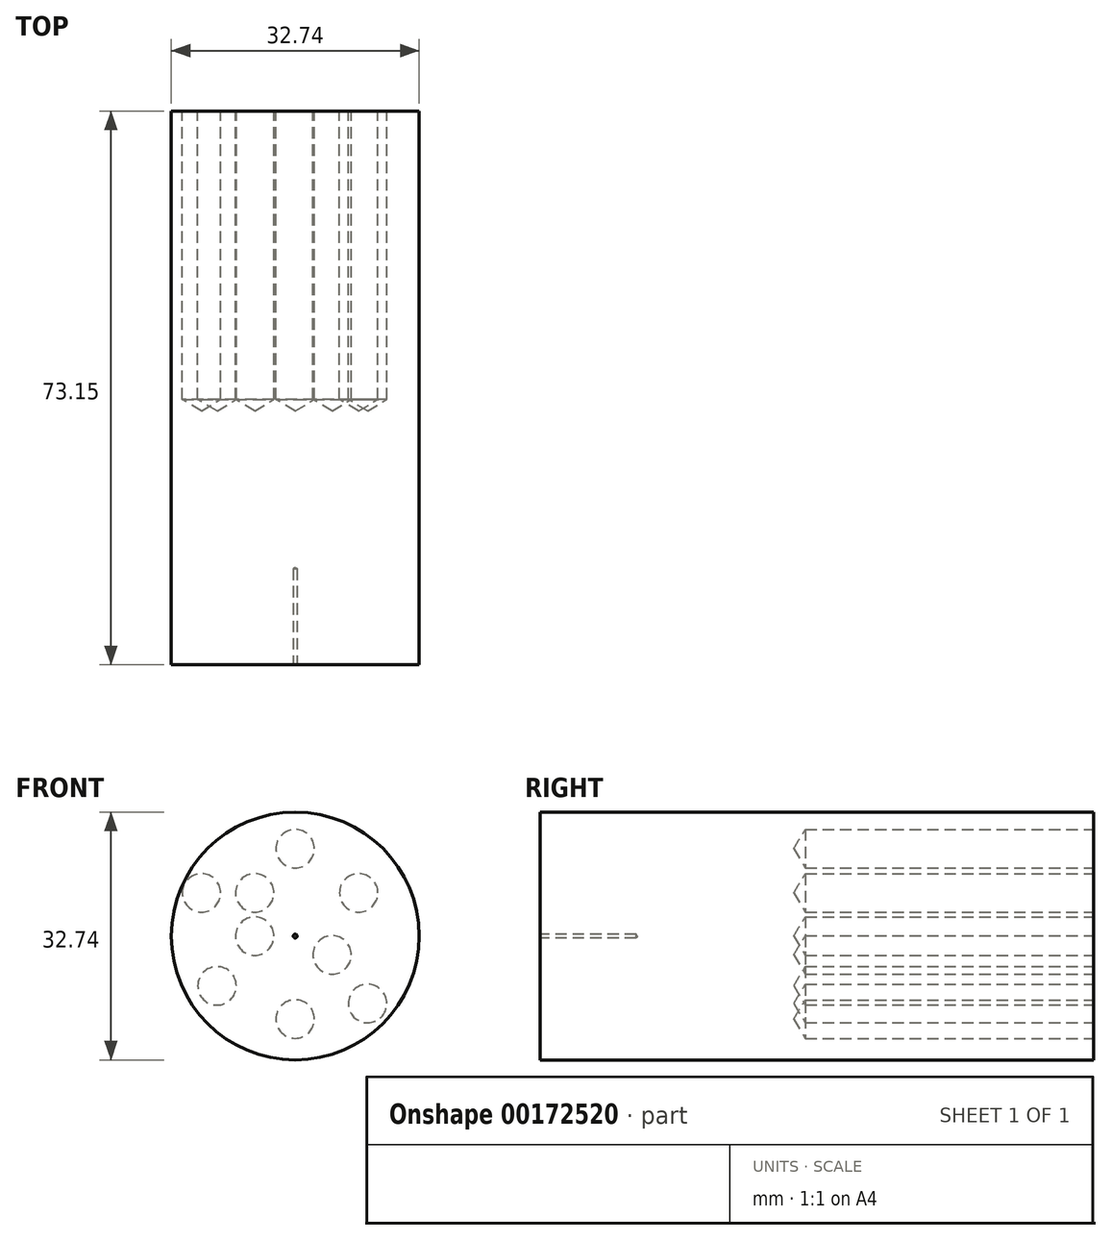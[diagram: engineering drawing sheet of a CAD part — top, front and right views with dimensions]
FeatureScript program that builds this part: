
annotation { "Feature Type Name" : "Feature", "Feature Type Description" : "" }
export const myFeature = defineFeature(function(context is Context, id is Id, definition is map)
    precondition{}
    {
        {
            var Q0;
            Q0=qCreatedBy(makeId("Front.planeOp"),FACE);
            var sketch = newSketch(context, id + "F0", { "sketchPlane" : qUnion([Q0])});
            skCircle(sketch, "E0", {"center": v(0, 0) * mm, "radius": 16.37 * mm});
            skSolve(sketch);
        }
        {
            var Q0;
            Q0=makeQuery(id+"F0.imprint","IMPRINT",FACE,{"disambiguationData":[TD([[makeQuery(id+"F0.imprint","IMPRINT",EDGE,{"derivedFrom":sQuery(id+"F0.wireOp",EDGE,"E0")}),1.0]])]});
            extrude(context, id + "F1", {"entities" : qUnion([Q0]), "depth" : 73.15 * mm});
        }
        {
            var Q0;
            Q0=makeQuery(id+"F1.opExtrude","CAP_FACE",FACE,{"disambiguationData":[OSD([sQuery(id+"F0.wireOp",EDGE,"E0")])],"isStart":false});
            var sketch = newSketch(context, id + "F2", { "sketchPlane" : qUnion([Q0])});
            skCircle(sketch, "E1", {"center": v(0, 0) * mm, "radius": 16.43 * mm});
            skSolve(sketch);
        }
        {
            var Q0;
            Q0=sQuery(id+"F2.wireOp",VERTEX,"E1.center");
            var Q1;
            Q1=makeQuery(id+"F1.opExtrude","SWEPT_BODY",BODY,{"disambiguationData":[OSD([sQuery(id+"F0.wireOp",EDGE,"E0")])]});
            hole(context, id + "F3", {"style" : HoleStyle.SIMPLE, "endStyle" : HoleEndStyle.BLIND, "holeDiameter" : 0.5 * mm, "holeDepth" : 12.7 * mm, "locations" : qUnion([Q0]), "scope" : qUnion([Q1])});
        }
        {
            var Q0;
            Q0=qCreatedBy(makeId("Front.planeOp"),FACE);
            var sketch = newSketch(context, id + "F4", { "sketchPlane" : qUnion([Q0])});
            skCircle(sketch, "E2", {"center": v(-5.36, 5.7) * mm, "radius": 5.2 * mm});
            skCircle(sketch, "E3", {"center": v(8.39, 5.7) * mm, "radius": 5.75 * mm});
            skCircle(sketch, "E4", {"center": v(4.88, -2.49) * mm, "radius": 7.96 * mm});
            skCircle(sketch, "E5", {"center": v(0, -10.97) * mm, "radius": 5.18 * mm});
            skCircle(sketch, "E6", {"center": v(9.56, -8.92) * mm, "radius": 4.37 * mm});
            skCircle(sketch, "E7", {"center": v(-5.36, 0) * mm, "radius": 5.15 * mm});
            skCircle(sketch, "E8", {"center": v(-10.34, -6.58) * mm, "radius": 6.05 * mm});
            skCircle(sketch, "E9", {"center": v(0, 11.56) * mm, "radius": 4.48 * mm});
            skCircle(sketch, "E10", {"center": v(-12.38, 5.7) * mm, "radius": 3.9 * mm});
            skSolve(sketch);
        }
        {
            var Q0;
            Q0=sQuery(id+"F4.wireOp",VERTEX,"E10.center");
            var Q1;
            Q1=sQuery(id+"F4.wireOp",VERTEX,"E2.center");
            var Q2;
            Q2=sQuery(id+"F4.wireOp",VERTEX,"E9.center");
            var Q3;
            Q3=sQuery(id+"F4.wireOp",VERTEX,"E3.center");
            var Q4;
            Q4=sQuery(id+"F4.wireOp",VERTEX,"E7.center");
            var Q5;
            Q5=sQuery(id+"F4.wireOp",VERTEX,"E4.center");
            var Q6;
            Q6=sQuery(id+"F4.wireOp",VERTEX,"E6.center");
            var Q7;
            Q7=sQuery(id+"F4.wireOp",VERTEX,"E5.center");
            var Q8;
            Q8=sQuery(id+"F4.wireOp",VERTEX,"E8.center");
            var Q9;
            Q9=makeQuery(id+"F1.opExtrude","SWEPT_BODY",BODY,{"disambiguationData":[OSD([sQuery(id+"F0.wireOp",EDGE,"E0")])]});
            hole(context, id + "F5", {"style" : HoleStyle.SIMPLE, "endStyle" : HoleEndStyle.BLIND, "oppositeDirection" : true, "holeDiameter" : 5.08 * mm, "holeDepth" : 38.1 * mm, "locations" : qUnion([Q0, Q1, Q2, Q3, Q4, Q5, Q6, Q7, Q8]), "scope" : qUnion([Q9])});
        }
    });
